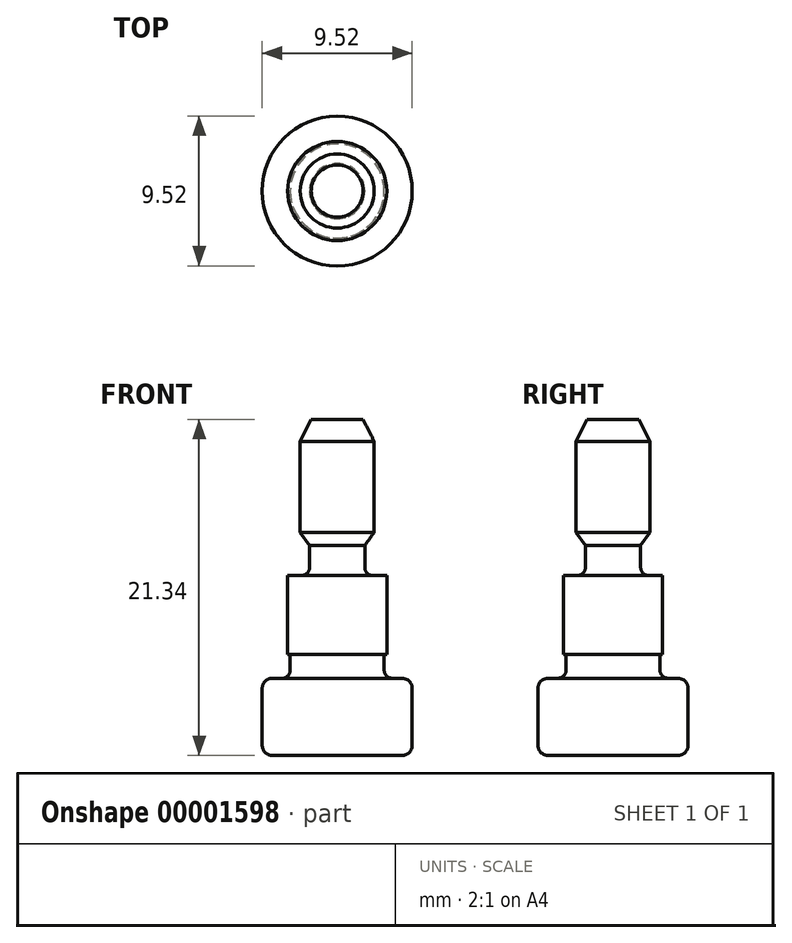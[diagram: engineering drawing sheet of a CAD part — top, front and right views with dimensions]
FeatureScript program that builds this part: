
annotation { "Feature Type Name" : "Feature", "Feature Type Description" : "" }
export const myFeature = defineFeature(function(context is Context, id is Id, definition is map)
    precondition{}
    {
        {
            var Q0;
            Q0=qCreatedBy(makeId("Front.planeOp"),FACE);
            var sketch = newSketch(context, id + "F0", { "sketchPlane" : qUnion([Q0])});
            skLineSegment(sketch, "E0", {"start": v(0, 0) * mm, "end": v(4.76, 0) * mm});
            skLineSegment(sketch, "E1", {"start": v(4.76, 0) * mm, "end": v(4.76, 4.9) * mm});
            skLineSegment(sketch, "E2", {"start": v(4.76, 4.9) * mm, "end": v(2.98, 4.9) * mm});
            skLineSegment(sketch, "E3", {"start": v(2.98, 4.9) * mm, "end": v(2.98, 6.43) * mm});
            skLineSegment(sketch, "E4", {"start": v(2.98, 6.43) * mm, "end": v(3.15, 6.43) * mm});
            skLineSegment(sketch, "E5", {"start": v(3.15, 6.43) * mm, "end": v(3.15, 11.43) * mm});
            skLineSegment(sketch, "E6", {"start": v(3.15, 11.43) * mm, "end": v(1.75, 11.43) * mm});
            skLineSegment(sketch, "E7", {"start": v(1.75, 11.43) * mm, "end": v(1.75, 13.34) * mm});
            skLineSegment(sketch, "E8", {"start": v(1.75, 13.33) * mm, "end": v(2.35, 14.17) * mm});
            skLineSegment(sketch, "E9", {"start": v(2.35, 14.17) * mm, "end": v(2.35, 19.94) * mm});
            skLineSegment(sketch, "E10", {"start": v(2.35, 19.94) * mm, "end": v(1.65, 21.34) * mm});
            skLineSegment(sketch, "E11", {"start": v(1.65, 21.34) * mm, "end": v(0, 21.34) * mm});
            skLineSegment(sketch, "E12", {"start": v(0, 21.34) * mm, "end": v(0, 0) * mm});
            skSolve(sketch);
        }
        {
            var Q0;
            Q0=makeQuery(id+"F0.imprint","IMPRINT",FACE,{"disambiguationData":[TD([[makeQuery(id+"F0.imprint","IMPRINT",EDGE,{"derivedFrom":sQuery(id+"F0.wireOp",EDGE,"E0")}),1.0]])]});
            var Q1;
            Q1=sQuery(id+"F0.wireOp",EDGE,"E12");
            revolve(context, id + "F1", {"entities" : qUnion([Q0]), "axis" : qUnion([Q1]), "revolveType" : RevolveType.FULL});
        }
        {
            var Q0;
            Q0=makeQuery(id+"F1.opRevolve","SWEPT_EDGE",EDGE,{"disambiguationData":[OSD([sQuery(id+"F0.wireOp",EDGE,"E2"),sQuery(id+"F0.wireOp",EDGE,"E3")])]});
            var Q1;
            Q1=makeQuery(id+"F1.opRevolve","SWEPT_EDGE",EDGE,{"disambiguationData":[OSD([sQuery(id+"F0.wireOp",EDGE,"E6"),sQuery(id+"F0.wireOp",EDGE,"E7")])]});
            fillet(context, id + "F2", {"entities" : qUnion([Q0, Q1]), "radius" : 0.5 * mm, "tangentPropagation" : true, "allowEdgeOverflow" : false});
        }
        {
            var Q0;
            Q0=makeQuery(id+"F1.opRevolve","SWEPT_EDGE",EDGE,{"disambiguationData":[OSD([sQuery(id+"F0.wireOp",EDGE,"E0"),sQuery(id+"F0.wireOp",EDGE,"E1")])]});
            var Q1;
            Q1=makeQuery(id+"F1.opRevolve","SWEPT_EDGE",EDGE,{"disambiguationData":[OSD([sQuery(id+"F0.wireOp",EDGE,"E1"),sQuery(id+"F0.wireOp",EDGE,"E2")])]});
            fillet(context, id + "F3", {"entities" : qUnion([Q0, Q1]), "radius" : 0.64 * mm, "tangentPropagation" : true, "allowEdgeOverflow" : false});
        }
    });
